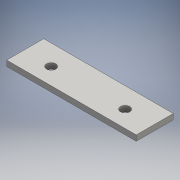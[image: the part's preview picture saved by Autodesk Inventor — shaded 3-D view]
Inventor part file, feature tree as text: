
AUTODESK INVENTOR PART (.ipt)
format: ipt  version: 2016 (Build 200138000, 138)  size: 95,744 bytes
history: native  units: mm
features: extrude x1, sketch x1
ambient origin geometry x8: Origin, YZ Plane, XZ Plane, XY Plane, X Axis, Y Axis, Z Axis, Center Point
bodies: Solid1 (feature_tree)
feature tree (2):
  extrude  "Extrusion1"  Depth=20.0mm
  sketch  "Sketch1"  dims[d0=70.0mm d1=20.0mm d2=5.0mm d3=5.0mm d4=15.0mm d5=40.0mm d6=3.0mm d7=0.0mm d8=9.0mm d9=9.0mm]
